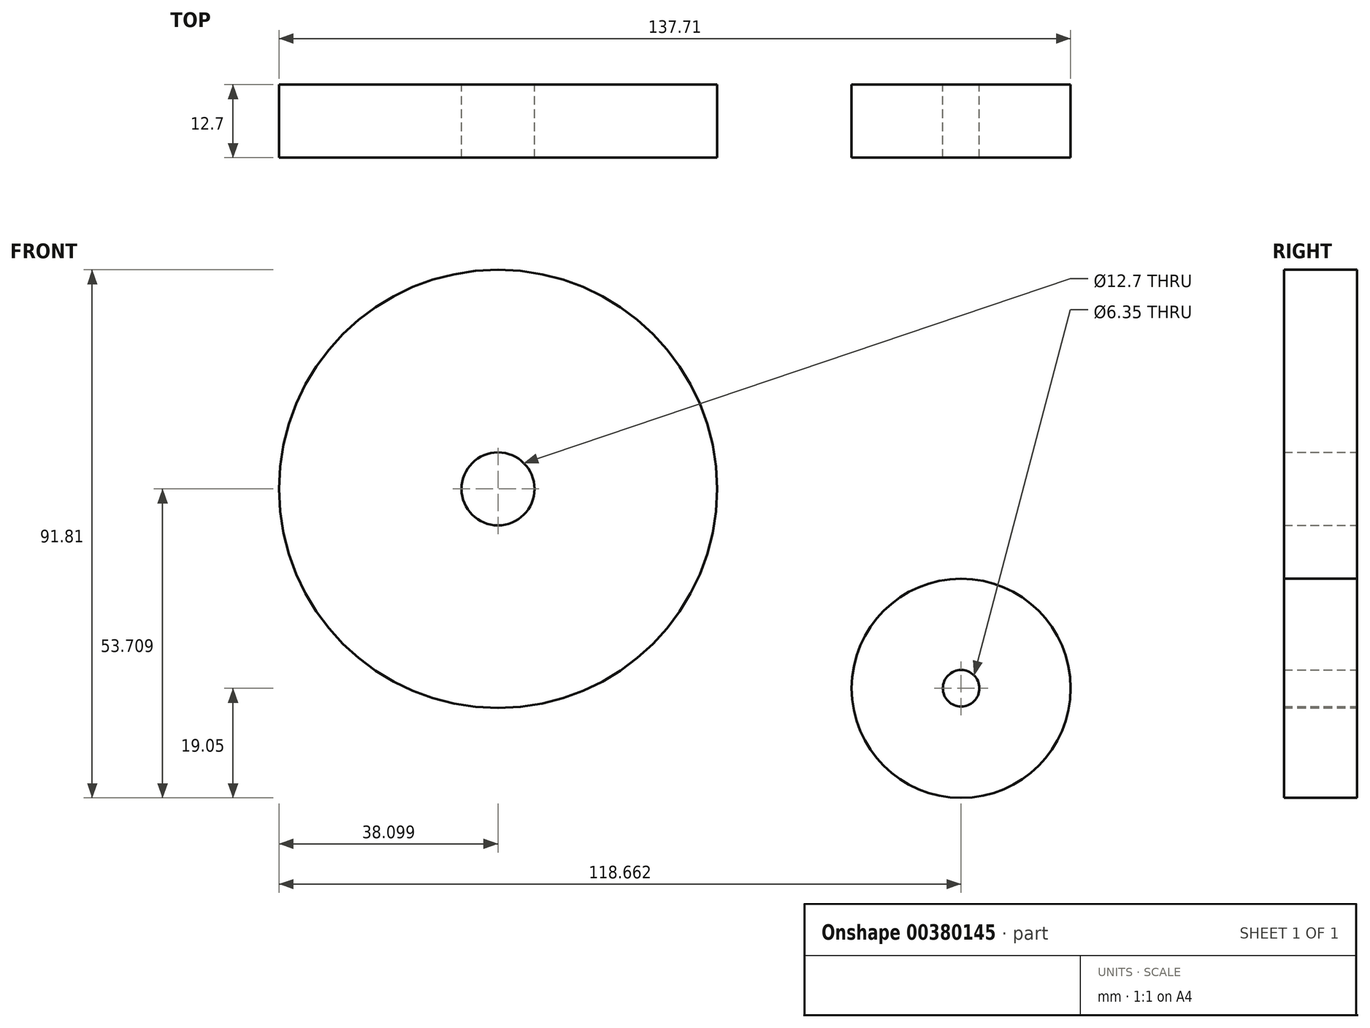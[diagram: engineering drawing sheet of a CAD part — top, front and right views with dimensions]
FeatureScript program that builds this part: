
annotation { "Feature Type Name" : "Feature", "Feature Type Description" : "" }
export const myFeature = defineFeature(function(context is Context, id is Id, definition is map)
    precondition{}
    {
        {
            var Q0;
            Q0=qCreatedBy(makeId("Front.planeOp"),FACE);
            var sketch = newSketch(context, id + "F0", { "sketchPlane" : qUnion([Q0])});
            skCircle(sketch, "E0", {"center": v(-39.82, 18.99) * mm, "radius": 38.1 * mm});
            skCircle(sketch, "E1", {"center": v(-39.82, 18.99) * mm, "radius": 6.35 * mm});
            skCircle(sketch, "E2", {"center": v(40.74, -15.67) * mm, "radius": 19.05 * mm});
            skCircle(sketch, "E3", {"center": v(40.74, -15.67) * mm, "radius": 3.18 * mm});
            skSolve(sketch);
        }
        {
            var Q0;
            Q0=makeQuery(id+"F0.imprint","IMPRINT",FACE,{"disambiguationData":[TD([[makeQuery(id+"F0.imprint","IMPRINT",EDGE,{"derivedFrom":sQuery(id+"F0.wireOp",EDGE,"E2")}),1.0]])]});
            var Q1;
            Q1=makeQuery(id+"F0.imprint","IMPRINT",FACE,{"disambiguationData":[TD([[makeQuery(id+"F0.imprint","IMPRINT",EDGE,{"derivedFrom":sQuery(id+"F0.wireOp",EDGE,"E0")}),1.0]])]});
            extrude(context, id + "F1", {"entities" : qUnion([Q0, Q1]), "depth" : 12.7 * mm});
        }
    });
